# Revit family: Sanitary_Toilets_Sanindusa_Sanlife-Rimflush-Wall-Mounted-Toilet
name_source: partatom
category: Plumbing Fixtures
revit_build: Autodesk Revit 2018 (Build: 20170223_1515(x64)
units: mm (PartAtom-declared; Revit-internal decimal feet)

## family parameters
Always vertical = Yes
Cut with Voids When Loaded = No
Host = Wall
OmniClass Number = 23.45.00.00
OmniClass Title = Sanitary, Laundry, and Cleaning Equipment
Part Type = Normal
Room Calculation Point = No
Round Connector Dimension = Use Diameter
Shared = No

## types (1)
- SANINDUSA_Rimflushwallmountedwcwithconcealedfixation_136032004_380x560x350_Sanlife
    AssetType = Fixed
    CodePerformance = EN 997:2012 CL 1 - 6 A
    Color = White
    Constituents = Compatible toilet seat (not included): 2363100-Toilet seat sanlife with clipoff and slowclose system. Compatible suport frames (not inluded): 411023-SANDOUBLE free standing frame w/ dual flushing cistern for wall hung WC, 4193311-SANSLIM build-in element w/dual flushing cistern, 41733xx-SANGLASS WALL external frame w/ dual flushing cistern for wall hung WC, 40333-SANFIX frame w/ dual flushing cistern for wall hung WC, 40323-SANFIX freestanding frame w/ dual flushing cistern for wall hung WC, 40233-SANFLUSH build-in element w/ dual flushing cistern for wall hung WC, 40633-SANSPACE frame w/ dual flushing cistern for wall hung WC, 40533-SANBEST build-in element w/ dual flushing cistern for wall hung WC. 4000-Fixing kit for wall mounted toilet (included)
    Cost = 0 $
    Description = Soil appliance for the disposal of excrement.
    DrainSize = 100 mm  [stored 0.328084 ft]
    Edition number = 1
    Features = Domestic and commercial use. With rimflush discharge system without rim, which promotes hygiene,
make easier the toilet cleaning and reduces the proliferation of germs. Toilet seat with clipoff system easy to clean and slow close.
    Finish = gloss
    InletDiameter = 50 mm  [stored 0.164042 ft]
    Installation Instructions = https://www.tec.sanindusa.pt
    InstallationDate = 1900-12-31T23:59:59
    ManufacturerName = Sanindusa
    ManufacturerURL = www.tec.sanindusa.pt
    Material = Vitreous China
    ModelNumber = 136032004
    ModelReference = Sanlife
    Name = Sanlife rimflush wall mounted wc
    NominalHeight = 350 mm  [stored 1.14829 ft]
    NominalLength = 380 mm
    NominalWidth = 560 mm  [stored 1.83727 ft]
    Product Guid = fb9f5053-9a22-469a-ac2c-3c9782664f03
    Product data url = https://bimobject.com
    ProductInformation = https://www.tec.sanindusa.pt
    ProductionYear = 2018
    Size = 380x560x350
    SustainabilityPerformance = n/a
n/a
    URL = www.tec.sanindusa.pt
    Uniclass2015Code = Pr_40_20_93_94
    Uniclass2015Title = WC pans
    Uniclass2015Version = Products v1.6
    Version = 1
    WarrantyDescription = https://www.tec.sanindusa.pt
    WarrantyDurationParts = 5
    WarrantyDurationUnit = year
    WarrantyStartDate = 1900-12-31T23:59:59
    Weight = 22.80 kg

note: [stored X ft] marks values corroborated as IEEE doubles in the binary element streams (Revit-internal decimal feet)

## geometry (parser evidence)
native form markers: Sweep x7
no freeform markers — native parametric forms only
